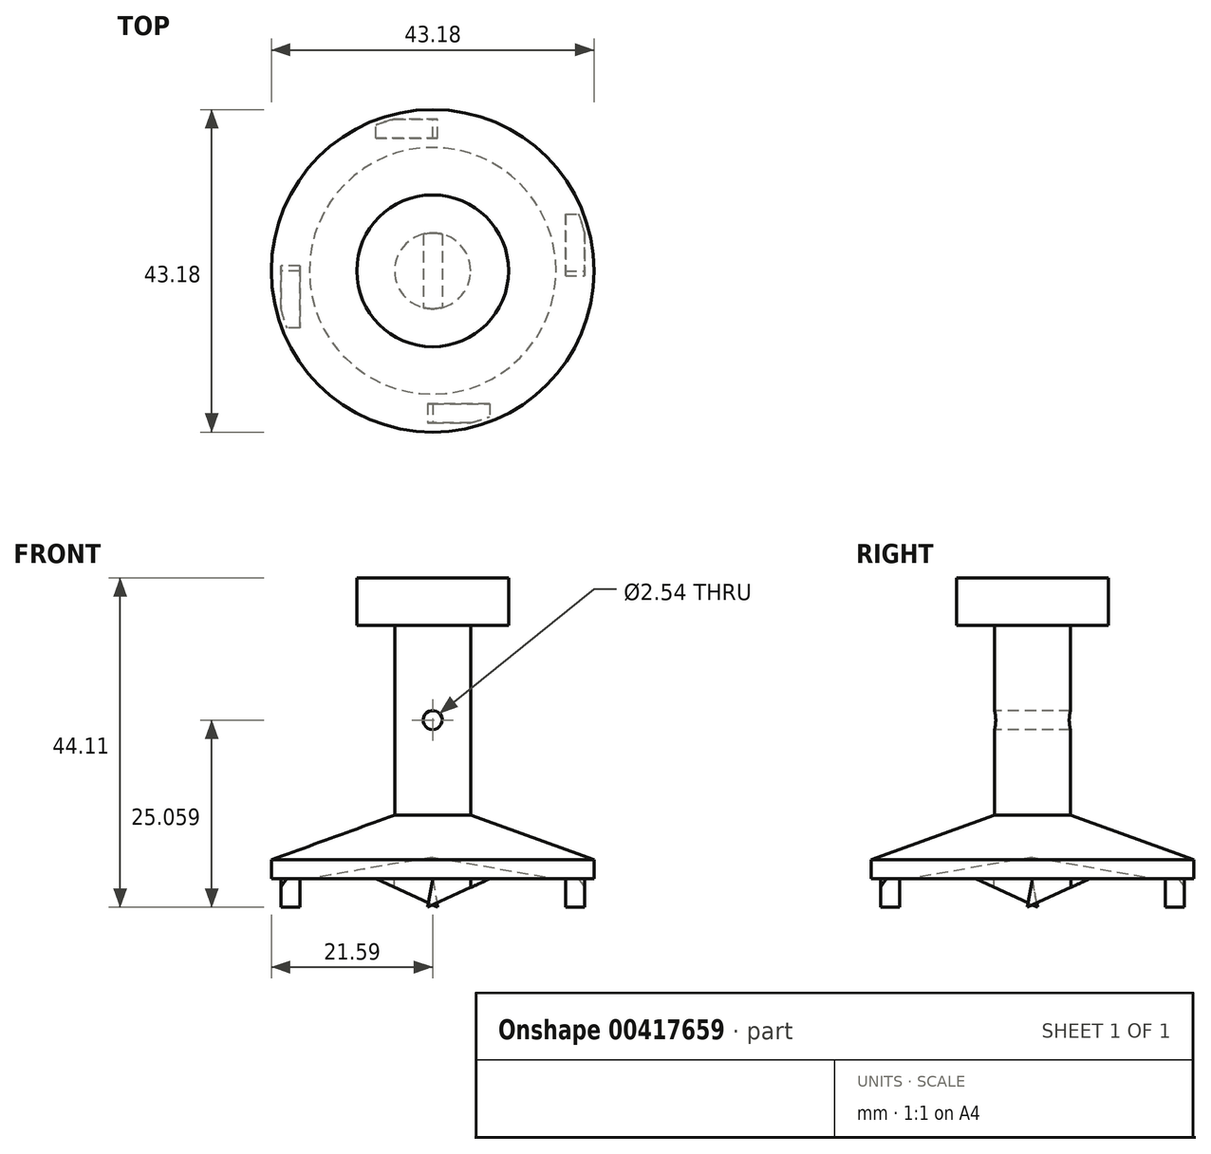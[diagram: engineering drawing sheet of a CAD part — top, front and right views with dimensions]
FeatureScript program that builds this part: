
annotation { "Feature Type Name" : "Feature", "Feature Type Description" : "" }
export const myFeature = defineFeature(function(context is Context, id is Id, definition is map)
    precondition{}
    {
        {
            var Q0;
            Q0=qCreatedBy(makeId("Front.planeOp"),FACE);
            cPlane(context, id + "F0", {"entities" : qUnion([Q0]), "cplaneType" : CPlaneType.OFFSET, "offset" : 20.32 * mm, "width" : 152.4 * mm, "height" : 152.4 * mm});
        }
        {
            var Q0;
            Q0=qCreatedBy(makeId("Front.planeOp"),FACE);
            cPlane(context, id + "F1", {"entities" : qUnion([Q0]), "cplaneType" : CPlaneType.OFFSET, "offset" : 20.32 * mm, "oppositeDirection" : true, "width" : 152.4 * mm, "height" : 152.4 * mm});
        }
        {
            var Q0;
            Q0=qCreatedBy(makeId("Right.planeOp"),FACE);
            cPlane(context, id + "F2", {"entities" : qUnion([Q0]), "cplaneType" : CPlaneType.OFFSET, "offset" : 20.32 * mm, "oppositeDirection" : true, "width" : 152.4 * mm, "height" : 152.4 * mm});
        }
        {
            var Q0;
            Q0=qCreatedBy(makeId("Right.planeOp"),FACE);
            cPlane(context, id + "F3", {"entities" : qUnion([Q0]), "cplaneType" : CPlaneType.OFFSET, "offset" : 20.32 * mm, "width" : 152.4 * mm, "height" : 152.4 * mm});
        }
        {
            var Q0;
            Q0=qCreatedBy(id+"F3.planeOp",FACE);
            var sketch = newSketch(context, id + "F4", { "sketchPlane" : qUnion([Q0])});
            skLineSegment(sketch, "E0", {"start": v(0, 0) * mm, "end": v(-0.67, -3.81) * mm});
            skLineSegment(sketch, "E1", {"start": v(-0.67, -3.81) * mm, "end": v(7.62, 0) * mm});
            skLineSegment(sketch, "E2", {"start": v(7.62, 0) * mm, "end": v(0, 0) * mm});
            skSolve(sketch);
        }
        {
            var Q0;
            Q0 = qSketchRegion(id + "F4", true);
            extrude(context, id + "F5", {"entities" : qUnion([Q0]), "oppositeDirection" : true, "depth" : 2.54 * mm});
        }
        {
            var Q0;
            Q0=qCreatedBy(id+"F2.planeOp",FACE);
            var sketch = newSketch(context, id + "F6", { "sketchPlane" : qUnion([Q0])});
            skLineSegment(sketch, "E3", {"start": v(0, 0) * mm, "end": v(-7.62, 0) * mm});
            skLineSegment(sketch, "E4", {"start": v(-7.62, 0) * mm, "end": v(0.67, -3.8) * mm});
            skLineSegment(sketch, "E5", {"start": v(0.67, -3.81) * mm, "end": v(0, 0) * mm});
            skSolve(sketch);
        }
        {
            var Q0;
            Q0 = qSketchRegion(id + "F6", true);
            extrude(context, id + "F7", {"entities" : qUnion([Q0]), "operationType" : NewBodyOperationType.ADD, "depth" : 2.54 * mm});
        }
        {
            var Q0;
            Q0=qCreatedBy(id+"F1.planeOp",FACE);
            var sketch = newSketch(context, id + "F8", { "sketchPlane" : qUnion([Q0])});
            skLineSegment(sketch, "E6", {"start": v(0, 0) * mm, "end": v(0.67, -3.81) * mm});
            skLineSegment(sketch, "E7", {"start": v(0.67, -3.81) * mm, "end": v(-7.62, 0) * mm});
            skLineSegment(sketch, "E8", {"start": v(-7.62, 0) * mm, "end": v(0, 0) * mm});
            skSolve(sketch);
        }
        {
            var Q0;
            Q0 = qSketchRegion(id + "F8", true);
            extrude(context, id + "F9", {"entities" : qUnion([Q0]), "operationType" : NewBodyOperationType.ADD, "depth" : 2.54 * mm});
        }
        {
            var Q0;
            Q0=qCreatedBy(id+"F0.planeOp",FACE);
            var sketch = newSketch(context, id + "F10", { "sketchPlane" : qUnion([Q0])});
            skLineSegment(sketch, "E9", {"start": v(0, 0) * mm, "end": v(7.62, 0) * mm});
            skLineSegment(sketch, "E10", {"start": v(7.62, 0) * mm, "end": v(-0.67, -3.81) * mm});
            skLineSegment(sketch, "E11", {"start": v(-0.67, -3.81) * mm, "end": v(0, 0) * mm});
            skSolve(sketch);
        }
        {
            var Q0;
            Q0 = qSketchRegion(id + "F10", true);
            extrude(context, id + "F11", {"entities" : qUnion([Q0]), "operationType" : NewBodyOperationType.ADD, "oppositeDirection" : true, "depth" : 2.54 * mm});
        }
        {
            var Q0;
            Q0=qCreatedBy(makeId("Front.planeOp"),FACE);
            var sketch = newSketch(context, id + "F12", { "sketchPlane" : qUnion([Q0])});
            skLineSegment(sketch, "E12", {"start": v(-16.51, 0) * mm, "end": v(0, 2.91) * mm});
            skLineSegment(sketch, "E13", {"start": v(0, 2.91) * mm, "end": v(16.51, 0) * mm});
            skLineSegment(sketch, "E14", {"start": v(16.51, 0) * mm, "end": v(21.6, 0) * mm});
            skLineSegment(sketch, "E15", {"start": v(21.6, 0) * mm, "end": v(5.08, 4.42) * mm});
            skLineSegment(sketch, "E16", {"start": v(5.08, 4.42) * mm, "end": v(5.08, 33.95) * mm});
            skLineSegment(sketch, "E17", {"start": v(5.08, 33.95) * mm, "end": v(10.16, 33.95) * mm});
            skLineSegment(sketch, "E18", {"start": v(10.16, 33.95) * mm, "end": v(10.16, 40.3) * mm});
            skLineSegment(sketch, "E19", {"start": v(10.16, 40.3) * mm, "end": v(-10.16, 40.3) * mm});
            skLineSegment(sketch, "E20", {"start": v(-10.16, 40.3) * mm, "end": v(-10.16, 33.95) * mm});
            skLineSegment(sketch, "E21", {"start": v(-10.16, 33.95) * mm, "end": v(-5.08, 33.95) * mm});
            skLineSegment(sketch, "E22", {"start": v(-5.08, 33.95) * mm, "end": v(-5.08, 8.55) * mm});
            skLineSegment(sketch, "E23", {"start": v(-21.6, 0) * mm, "end": v(-16.51, 0) * mm});
            skLineSegment(sketch, "E24", {"start": v(0, 2.91) * mm, "end": v(0, 44.35) * mm});
            skPoint(sketch, "E24.endSnap0", {"position": v(0, 40.3) * mm});
            skLineSegment(sketch, "E25", {"start": v(-21.6, 0) * mm, "end": v(-21.6, 2.54) * mm});
            skLineSegment(sketch, "E26", {"start": v(-21.6, 2.54) * mm, "end": v(-5.08, 8.55) * mm});
            skSolve(sketch);
        }
        {
            var Q0;
            {var subQ4=sQuery(id+"F12.wireOp",EDGE,"E12");Q0=makeQuery(id+"F12.imprint","IMPRINT",FACE,{"disambiguationData":[TD([[makeQuery(id+"F12.imprint","IMPRINT",EDGE,{"derivedFrom":subQ4}),1.0]])]});}
            var Q1;
            Q1=sQuery(id+"F12.wireOp",EDGE,"E24");
            revolve(context, id + "F13", {"operationType" : NewBodyOperationType.ADD, "entities" : qUnion([Q0]), "axis" : qUnion([Q1]), "revolveType" : RevolveType.FULL});
        }
        {
            var Q0;
            Q0=qCreatedBy(id+"F0.planeOp",FACE);
            var sketch = newSketch(context, id + "F14", { "sketchPlane" : qUnion([Q0])});
            skCircle(sketch, "E27", {"center": v(0, 21.25) * mm, "radius": 1.27 * mm});
            skSolve(sketch);
        }
        {
            var Q0;
            Q0=makeQuery(id+"F14.imprint","IMPRINT",FACE,{"disambiguationData":[TD([[makeQuery(id+"F14.imprint","IMPRINT",EDGE,{"derivedFrom":sQuery(id+"F14.wireOp",EDGE,"E27")}),1.0]])]});
            extrude(context, id + "F15", {"entities" : qUnion([Q0]), "operationType" : NewBodyOperationType.REMOVE, "oppositeDirection" : true, "depth" : 30.07 * mm});
        }
        {
            var Q0;
            Q0=qCreatedBy(makeId("Top.planeOp"),FACE);
            var sketch = newSketch(context, id + "F16", { "sketchPlane" : qUnion([Q0])});
            skCircle(sketch, "E28", {"center": v(0, 0) * mm, "radius": 20.96 * mm});
            skCircle(sketch, "E29", {"center": v(0, 0) * mm, "radius": 42.41 * mm});
            skSolve(sketch);
        }
        {
            var Q0;
            Q0 = qSketchRegion(id + "F16", true);
            extrude(context, id + "F17", {"entities" : qUnion([Q0]), "operationType" : NewBodyOperationType.REMOVE, "oppositeDirection" : true, "depth" : 25.4 * mm});
        }
    });
